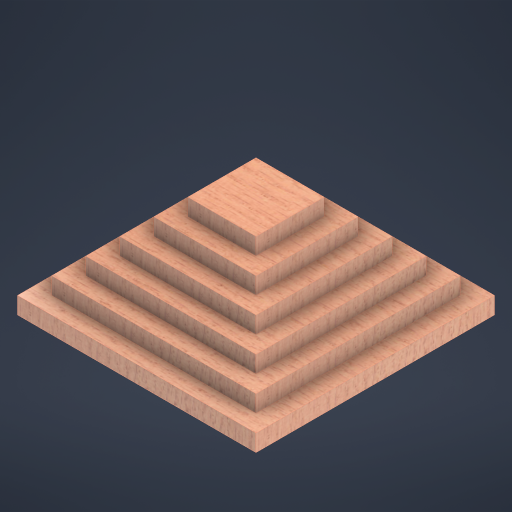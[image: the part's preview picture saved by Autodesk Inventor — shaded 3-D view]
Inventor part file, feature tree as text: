
AUTODESK INVENTOR PART (.ipt)
format: ipt  version: 2023 (Build 270158000, 158)  size: 491,008 bytes
history: native  units: mm
features: extrude x9, sketch x9, other x1
ambient origin geometry x8: Origin, YZ Plane, XZ Plane, XY Plane, X Axis, Y Axis, Z Axis, Center Point
bodies: Body1 (feature_tree)
feature tree (19):
  other  "Těleso1"
  extrude  "Vysunutí1"  Depth=210.0mm
  extrude  "Vysunutí2"  Depth=210.0mm
  extrude  "Vysunutí3"  Depth=15.0mm TaperAngle=0.0deg
  extrude  "Vysunutí4"  Depth=180.0mm
  extrude  "Vysunutí5"  Depth=180.0mm
  extrude  "Vysunutí6"  Depth=15.0mm TaperAngle=0.0deg
  extrude  "Vysunutí7"  Depth=150.0mm
  extrude  "Vysunutí8"  Depth=150.0mm
  extrude  "Vysunutí9"  Depth=15.0mm TaperAngle=0.0deg
  sketch  "Náčrt1"
  sketch  "Náčrt2"
  sketch  "Náčrt3"
  sketch  "Náčrt4"
  sketch  "Náčrt5"
  sketch  "Náčrt7"
  sketch  "Náčrt8"
  sketch  "Náčrt9"
  sketch  "Náčrt10"
